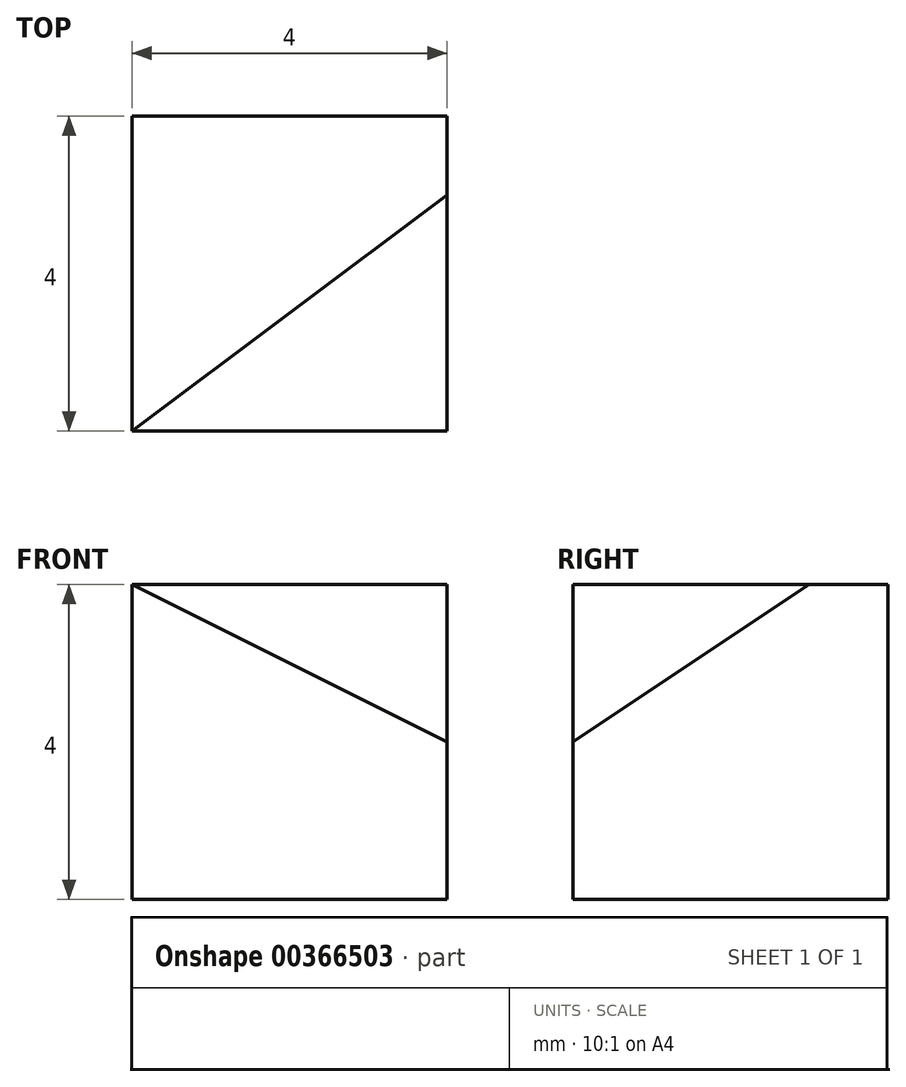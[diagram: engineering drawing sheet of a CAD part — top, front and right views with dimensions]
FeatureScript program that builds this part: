
annotation { "Feature Type Name" : "Feature", "Feature Type Description" : "" }
export const myFeature = defineFeature(function(context is Context, id is Id, definition is map)
    precondition{}
    {
        {
            var Q0;
            Q0=qCreatedBy(makeId("Front.planeOp"),FACE);
            var sketch = newSketch(context, id + "F0", { "sketchPlane" : qUnion([Q0])});
            skLineSegment(sketch, "E0", {"start": v(0, 0) * mm, "end": v(4, 0) * mm});
            skLineSegment(sketch, "E1", {"start": v(4, 0) * mm, "end": v(4, 4) * mm});
            skLineSegment(sketch, "E2", {"start": v(4, 4) * mm, "end": v(0, 4) * mm});
            skLineSegment(sketch, "E3", {"start": v(0, 4) * mm, "end": v(0, 0) * mm});
            skSolve(sketch);
        }
        {
            var Q0;
            Q0=makeQuery(id+"F0.imprint","IMPRINT",FACE,{"disambiguationData":[TD([[makeQuery(id+"F0.imprint","IMPRINT",EDGE,{"derivedFrom":sQuery(id+"F0.wireOp",EDGE,"E0")}),1.0]])]});
            extrude(context, id + "F1", {"entities" : qUnion([Q0]), "depth" : 4 * mm});
        }
        {
            var Q0;
            Q0=makeQuery(id+"F1.opExtrude","CAP_FACE",FACE,{"disambiguationData":[OSD([sQuery(id+"F0.wireOp",EDGE,"E0"),sQuery(id+"F0.wireOp",EDGE,"E1"),sQuery(id+"F0.wireOp",EDGE,"E2"),sQuery(id+"F0.wireOp",EDGE,"E3")])],"isStart":false});
            var sketch = newSketch(context, id + "F2", { "sketchPlane" : qUnion([Q0])});
            skLineSegment(sketch, "E4", {"start": v(4, 0) * mm, "end": v(4, 2) * mm});
            skLineSegment(sketch, "E5", {"start": v(4, 2) * mm, "end": v(0, 4) * mm});
            skSolve(sketch);
        }
        {
            var Q0;
            Q0=makeQuery(id+"F1.opExtrude","SWEPT_FACE",FACE,{"disambiguationData":[OSD([sQuery(id+"F0.wireOp",EDGE,"E2")])]});
            var sketch = newSketch(context, id + "F3", { "sketchPlane" : qUnion([Q0])});
            skLineSegment(sketch, "E6", {"start": v(4, -1) * mm, "end": v(0, -4) * mm});
            skLineSegment(sketch, "E7", {"start": v(4, -1) * mm, "end": v(4, 0) * mm});
            skSolve(sketch);
        }
        {
            var Q0;
            Q0=sQuery(id+"F3.wireOp",VERTEX,"E7.start");
            var Q1;
            Q1=sQuery(id+"F2.wireOp",VERTEX,"E5.end");
            var Q2;
            Q2=sQuery(id+"F2.wireOp",VERTEX,"E5.start");
            cPlane(context, id + "F4", {"entities" : qUnion([Q0, Q1, Q2]), "cplaneType" : CPlaneType.THREE_POINT, "offset" : 25 * mm, "width" : 150 * mm, "height" : 150 * mm});
        }
        {
            var Q0;
            Q0=qCreatedBy(id+"F4.planeOp",FACE);
            var sketch = newSketch(context, id + "F5", { "sketchPlane" : qUnion([Q0])});
            skPoint(sketch, "E8.0", {"position": v(-2.13, 1.1) * mm});
            skPoint(sketch, "E8.1", {"position": v(2.2, 2.22) * mm});
            skPoint(sketch, "E8.2", {"position": v(2.2, -1.39) * mm});
            skLineSegment(sketch, "E9", {"start": v(2.2, -1.39) * mm, "end": v(-2.13, 1.1) * mm});
            skLineSegment(sketch, "E10", {"start": v(-2.13, 1.1) * mm, "end": v(2.2, 2.22) * mm});
            skLineSegment(sketch, "E11", {"start": v(2.2, 2.22) * mm, "end": v(2.2, -1.39) * mm});
            skSolve(sketch);
        }
        {
            var Q0;
            Q0=qSketchRegion(id+"F5",true);
            extrude(context, id + "F6", {"entities" : qUnion([Q0]), "operationType" : NewBodyOperationType.REMOVE, "oppositeDirection" : true, "depth" : 25 * mm});
        }
    });
